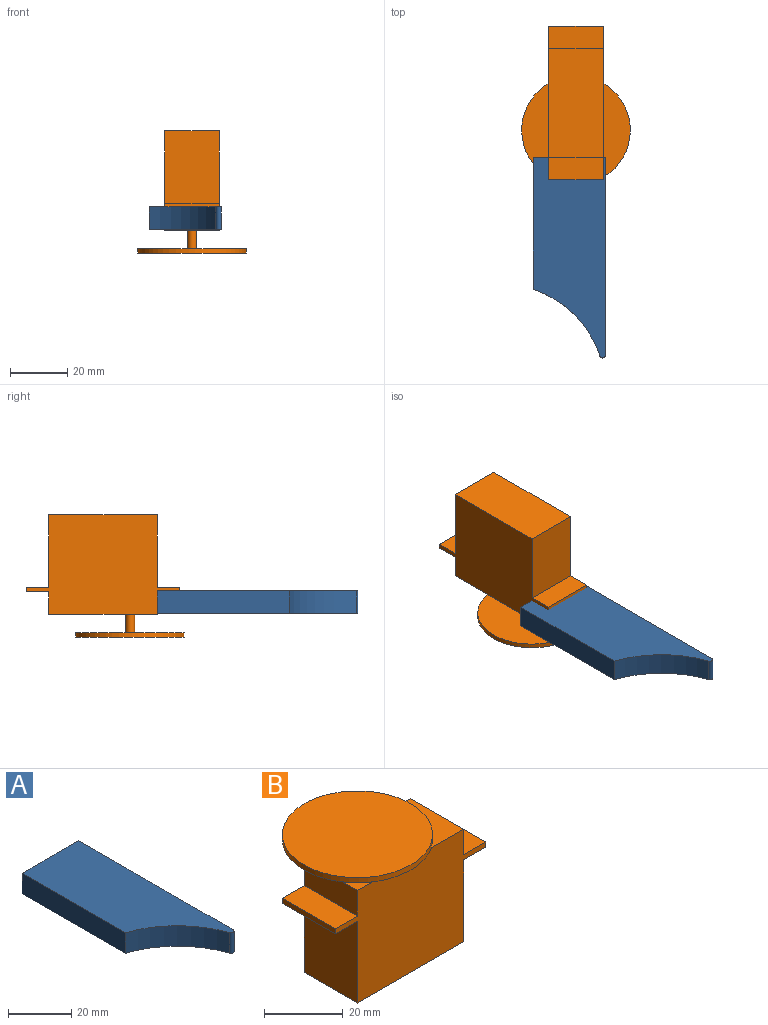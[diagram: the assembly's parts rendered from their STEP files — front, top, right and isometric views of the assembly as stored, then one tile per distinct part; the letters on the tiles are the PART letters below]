
ASSEMBLY  parts=2 mates=1
PART A: 7 faces, bbox 25.4x70.4x8 mm
  f0: cylinder r=37.21mm len=23.45mm, axis (0,0,-1), area 273mm2, adj f3,f4,f5,f6
  f1: plane 69.35x7.95mm, normal (1,0,0), area 551.3mm2, adj f2,f4,f5,f6
  f2: plane 25.4x7.95mm, normal (0,1,0), area 201.9mm2, adj f1,f3,f4,f5
  f3: plane 46.27x7.95mm, normal (-1,0,0), area 367.9mm2, adj f0,f2,f4,f5
  f4: plane 70.35x25.4mm, normal (0,0,1), area 1409.3mm2, adj f0,f1,f2,f3,f6
  f5: plane 70.35x25.4mm, normal (0,0,-1), area 1409.3mm2, adj f0,f1,f2,f3,f6
  f6: cylinder r=1mm len=7.95mm, axis (0,0,-1), area 22.4mm2, adj f0,f1,f4,f5
PART B: 18 faces, bbox 55.6x38.1x42.9 mm
  f0: plane 19.05x1.59mm, normal (-1,0,0), area 30.2mm2, adj f1,f5,f6,f9
  f1: plane 53.98x34.93mm, normal (0,-1,0), area 1355.8mm2, adj f0,f2,f3,f4,f6,f7,f8,f9
  f2: plane 19.05x1.59mm, normal (1,0,0), area 30.2mm2, adj f1,f5,f10,f12
  f3: plane 38.1x19.05mm, normal (0,0,-1), area 725.8mm2, adj f1,f5,f8,f11
  f4: plane 38.1x19.05mm, normal (0,0,1), area 717.9mm2, adj f1,f5,f7,f13,f14
  f5: plane 53.98x34.93mm, normal (0,1,0), area 1355.8mm2, adj f0,f2,f3,f4,f6,f7,f8,f9
  f6: plane 19.05x7.94mm, normal (0,0,1), area 151.2mm2, adj f0,f1,f5,f7
  f7: plane 19.05x7.94mm, normal (-1,0,0), area 151.2mm2, adj f1,f4,f5,f6
  f8: plane 25.4x19.05mm, normal (-1,0,0), area 483.9mm2, adj f1,f3,f5,f9
  f9: plane 19.05x7.94mm, normal (0,0,-1), area 151.2mm2, adj f0,f1,f5,f8
  f10: plane 19.05x7.94mm, normal (0,0,-1), area 151.2mm2, adj f1,f2,f5,f11
  f11: plane 25.4x19.05mm, normal (1,0,0), area 483.9mm2, adj f1,f3,f5,f10
  f12: plane 19.05x7.94mm, normal (0,0,1), area 151.2mm2, adj f1,f2,f5,f13
  f13: plane 19.05x7.94mm, normal (1,0,0), area 151.2mm2, adj f1,f4,f5,f12
  f14: cylinder r=1.59mm len=6.35mm, axis (0,0,-1), area 63.3mm2, adj f4,f17
  f15: cylinder r=19.05mm len=38.1mm, axis (0,0,-1), area 190mm2, adj f16,f17
  f16: plane 38.1x38.1mm, normal (0,0,1), area 1140.1mm2, adj f15
  f17: plane 38.1x38.1mm, normal (0,0,-1), area 1132.2mm2, adj f14,f15
PLACE A t=(-43.06,64.95,-66.57)mm
PLACE B rot(axis=(-0.71,-0.71,0),180deg) t=(-35.16,103.29,-57.39)mm
MATE planar B.f7 <-> A.f2  axis (0,-1,0) through (-44.68,111.23,-62.95)mm
